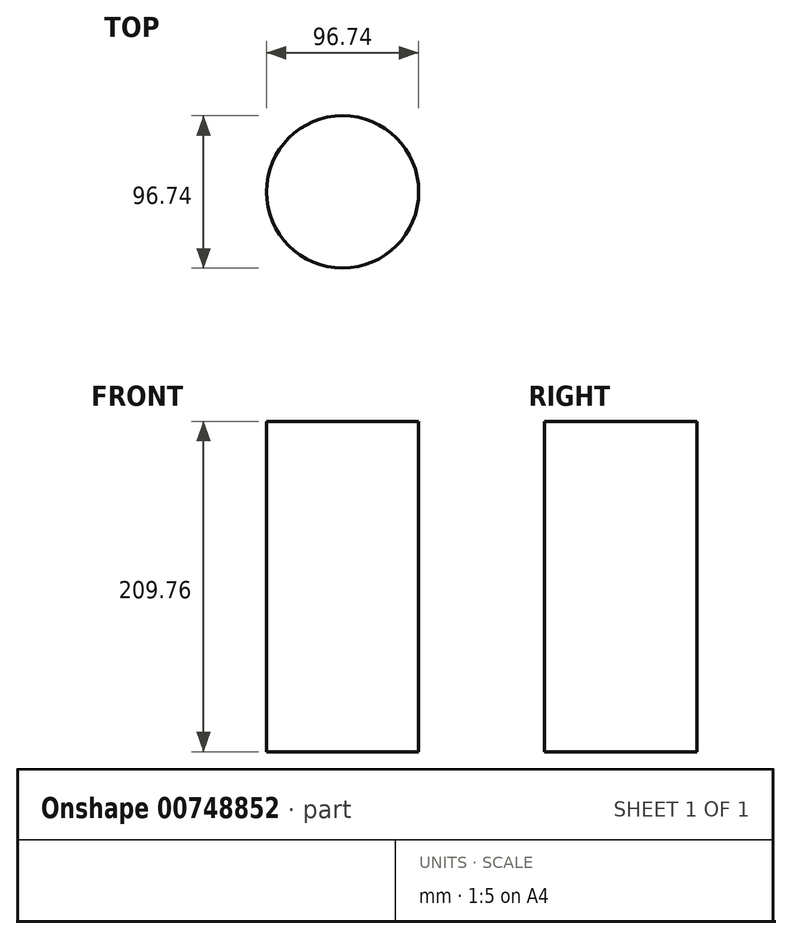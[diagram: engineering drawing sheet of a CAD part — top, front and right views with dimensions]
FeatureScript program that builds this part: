
annotation { "Feature Type Name" : "Feature", "Feature Type Description" : "" }
export const myFeature = defineFeature(function(context is Context, id is Id, definition is map)
    precondition{}
    {
        {
            var Q0;
            Q0=qCreatedBy(makeId("Top.planeOp"),FACE);
            var sketch = newSketch(context, id + "F0", { "sketchPlane" : qUnion([Q0])});
            skCircle(sketch, "E0", {"center": v(0, 0) * mm, "radius": 48.37 * mm});
            skSolve(sketch);
        }
        {
            var Q0;
            Q0=makeQuery(id+"F0.imprint","IMPRINT",FACE,{"disambiguationData":[TD([[makeQuery(id+"F0.imprint","IMPRINT",EDGE,{"derivedFrom":sQuery(id+"F0.wireOp",EDGE,"E0")}),1.0]])]});
            extrude(context, id + "F1", {"entities" : qUnion([Q0]), "depth" : 209.76 * mm, "offsetDistance" : 25.4 * mm});
        }
    });
